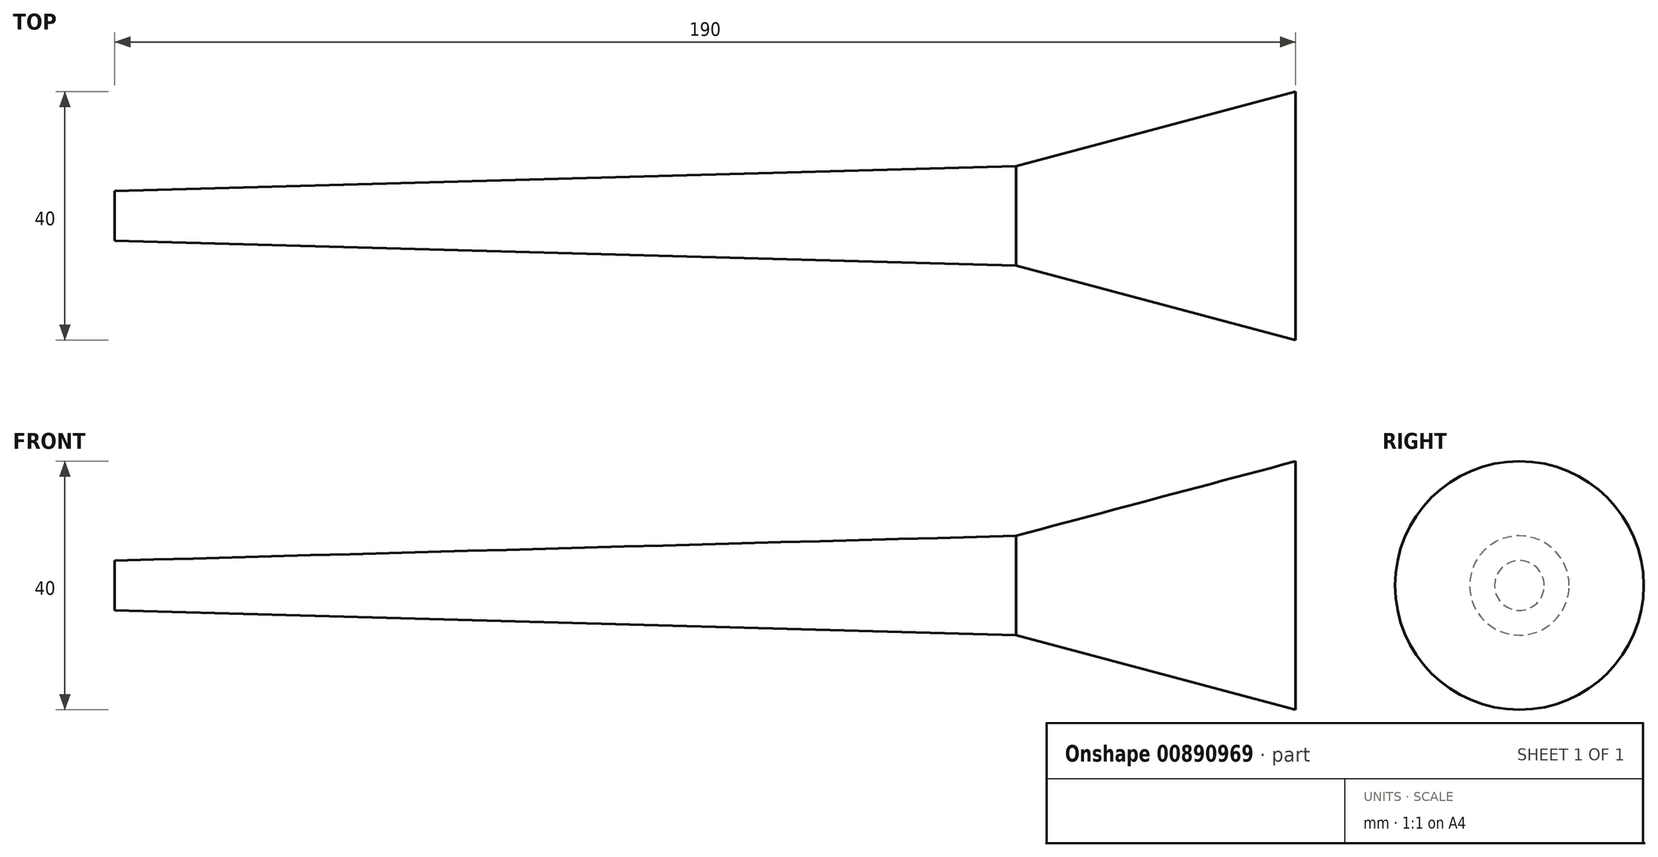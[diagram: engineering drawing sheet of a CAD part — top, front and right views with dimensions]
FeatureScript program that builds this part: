
annotation { "Feature Type Name" : "Feature", "Feature Type Description" : "" }
export const myFeature = defineFeature(function(context is Context, id is Id, definition is map)
    precondition{}
    {
        {
            var Q0;
            Q0=qCreatedBy(makeId("Top.planeOp"),FACE);
            var sketch = newSketch(context, id + "F0", { "sketchPlane" : qUnion([Q0])});
            skLineSegment(sketch, "E0.bottom", {"start": v(-94.08, 0) * mm, "end": v(50.92, 0) * mm});
            skLineSegment(sketch, "E0.left", {"start": v(-94.08, 0) * mm, "end": v(-94.08, 4) * mm});
            skLineSegment(sketch, "E0.right", {"start": v(50.92, 0) * mm, "end": v(50.92, 8) * mm});
            skLineSegment(sketch, "E1", {"start": v(-113.5, 0) * mm, "end": v(98.19, 0) * mm});
            skLineSegment(sketch, "E2", {"start": v(50.92, 8) * mm, "end": v(95.92, 20) * mm});
            skLineSegment(sketch, "E3", {"start": v(95.92, 20) * mm, "end": v(95.92, 0) * mm});
            skLineSegment(sketch, "E4", {"start": v(95.92, 0) * mm, "end": v(50.92, 0) * mm});
            skLineSegment(sketch, "E5", {"start": v(50.92, 8) * mm, "end": v(-94.08, 4) * mm});
            skPoint(sketch, "E0.top.start.orphan", {"position": v(-94.08, 8) * mm});
            skSolve(sketch);
        }
        {
            var Q0;
            Q0 = qSketchRegion(id + "F0", true);
            var Q1;
            Q1=sQuery(id+"F0.wireOp",EDGE,"E1");
            revolve(context, id + "F1", {"surfaceOperationType" : NewSurfaceOperationType.NEW, "entities" : qUnion([Q0]), "axis" : qUnion([Q1]), "revolveType" : RevolveType.FULL});
        }
    });
